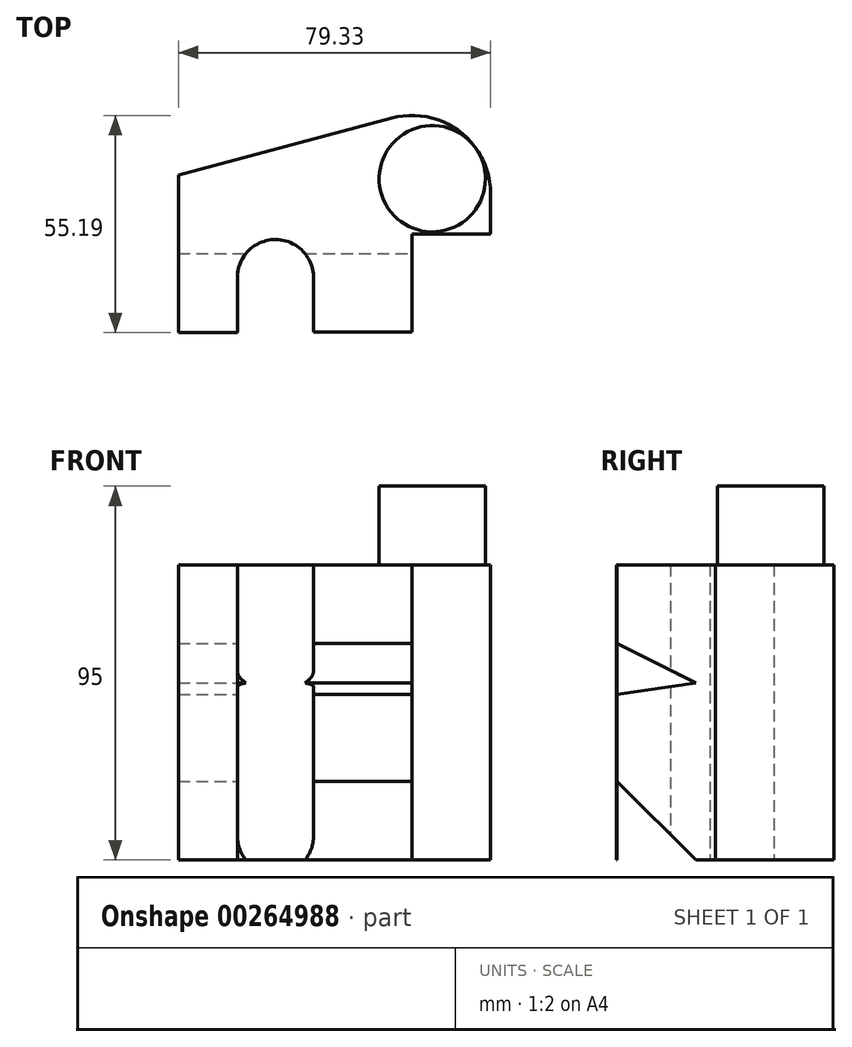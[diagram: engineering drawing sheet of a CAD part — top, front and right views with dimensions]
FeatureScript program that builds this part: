
annotation { "Feature Type Name" : "Feature", "Feature Type Description" : "" }
export const myFeature = defineFeature(function(context is Context, id is Id, definition is map)
    precondition{}
    {
        {
            var Q0;
            Q0=qCreatedBy(makeId("Top.planeOp"),FACE);
            var sketch = newSketch(context, id + "F0", { "sketchPlane" : qUnion([Q0])});
            skLineSegment(sketch, "E0", {"start": v(-54.15, 12.26) * mm, "end": v(-54.15, -27.74) * mm});
            skLineSegment(sketch, "E1", {"start": v(-54.15, -27.74) * mm, "end": v(-39.15, -27.74) * mm});
            skLineSegment(sketch, "E2", {"start": v(-19.82, -27.63) * mm, "end": v(5.18, -27.63) * mm});
            skLineSegment(sketch, "E3", {"start": v(5.18, -27.63) * mm, "end": v(5.18, -2.63) * mm});
            skLineSegment(sketch, "E4", {"start": v(5.18, -2.63) * mm, "end": v(25.18, -2.63) * mm});
            skLineSegment(sketch, "E5", {"start": v(-39.15, -27.74) * mm, "end": v(-39.15, -13.74) * mm});
            skLineSegment(sketch, "E6", {"start": v(-54.15, 12.26) * mm, "end": v(0, 26.77) * mm});
            skLineSegment(sketch, "E7", {"start": v(-19.82, -27.63) * mm, "end": v(-19.82, -14.1) * mm});
            skLineSegment(sketch, "E8", {"start": v(25.18, -2.63) * mm, "end": v(25.18, 7.45) * mm});
            skArc(sketch, "E9", {"start": v(0, 26.77) * mm, "mid": v(17.35, 23.31) * mm, "end": v(25.18, 7.45) * mm});
            skArc(sketch, "E10", {"start": v(-39.15, -13.74) * mm, "mid": v(-29.3, -4.08) * mm, "end": v(-19.82, -14.1) * mm});
            skSolve(sketch);
        }
        {
            var Q0;
            Q0=makeQuery(id+"F0.imprint","IMPRINT",FACE,{"disambiguationData":[TD([[makeQuery(id+"F0.imprint","IMPRINT",EDGE,{"derivedFrom":sQuery(id+"F0.wireOp",EDGE,"E0")}),1.0]])]});
            extrude(context, id + "F1", {"entities" : qUnion([Q0]), "depth" : 75 * mm});
        }
        {
            var Q0;
            Q0=makeQuery(id+"F1.opExtrude","CAP_FACE",FACE,{"disambiguationData":[OSD([sQuery(id+"F0.wireOp",EDGE,"E0"),sQuery(id+"F0.wireOp",EDGE,"E1"),sQuery(id+"F0.wireOp",EDGE,"E2"),sQuery(id+"F0.wireOp",EDGE,"E3"),sQuery(id+"F0.wireOp",EDGE,"E4"),sQuery(id+"F0.wireOp",EDGE,"E5"),sQuery(id+"F0.wireOp",EDGE,"E6"),sQuery(id+"F0.wireOp",EDGE,"E7"),sQuery(id+"F0.wireOp",EDGE,"E8"),sQuery(id+"F0.wireOp",EDGE,"E9"),sQuery(id+"F0.wireOp",EDGE,"E10")])],"isStart":false});
            var sketch = newSketch(context, id + "F2", { "sketchPlane" : qUnion([Q0])});
            skCircle(sketch, "E11", {"center": v(10.36, 11.37) * mm, "radius": 13.5 * mm});
            skSolve(sketch);
        }
        {
            var Q0;
            Q0=makeQuery(id+"F2.imprint","IMPRINT",FACE,{"disambiguationData":[TD([[makeQuery(id+"F2.imprint","IMPRINT",EDGE,{"derivedFrom":sQuery(id+"F2.wireOp",EDGE,"E11")}),1.0]])]});
            var Q1;
            Q1=sQuery(id+"F2.wireOp",EDGE,"E11");
            extrude(context, id + "F3", {"entities" : qUnion([Q0]), "operationType" : NewBodyOperationType.ADD, "surfaceEntities" : qUnion([Q1]), "depth" : 20 * mm});
        }
        {
            var Q0;
            Q0=makeQuery(id+"F1.opExtrude","SWEPT_FACE",FACE,{"disambiguationData":[OSD([sQuery(id+"F0.wireOp",EDGE,"E3")])]});
            var sketch = newSketch(context, id + "F4", { "sketchPlane" : qUnion([Q0])});
            skLineSegment(sketch, "E12", {"start": v(-27.63, 20) * mm, "end": v(-7.63, 0) * mm});
            skLineSegment(sketch, "E13", {"start": v(-27.63, 55) * mm, "end": v(-7.63, 45) * mm});
            skLineSegment(sketch, "E14", {"start": v(-7.63, 45) * mm, "end": v(-27.63, 42.03) * mm});
            skLineSegment(sketch, "E15", {"start": v(-27.63, 55) * mm, "end": v(-27.63, 42.03) * mm});
            skLineSegment(sketch, "E16", {"start": v(-27.63, 20) * mm, "end": v(-27.63, 0) * mm});
            skLineSegment(sketch, "E17", {"start": v(-27.63, 0) * mm, "end": v(-7.63, 0) * mm});
            skSolve(sketch);
        }
        {
            var Q0;
            Q0 = qSketchRegion(id + "F4", true);
            extrude(context, id + "F5", {"entities" : qUnion([Q0]), "operationType" : NewBodyOperationType.REMOVE, "endBound" : BoundingType.THROUGH_ALL, "oppositeDirection" : true, "depth" : 25 * mm});
        }
    });
